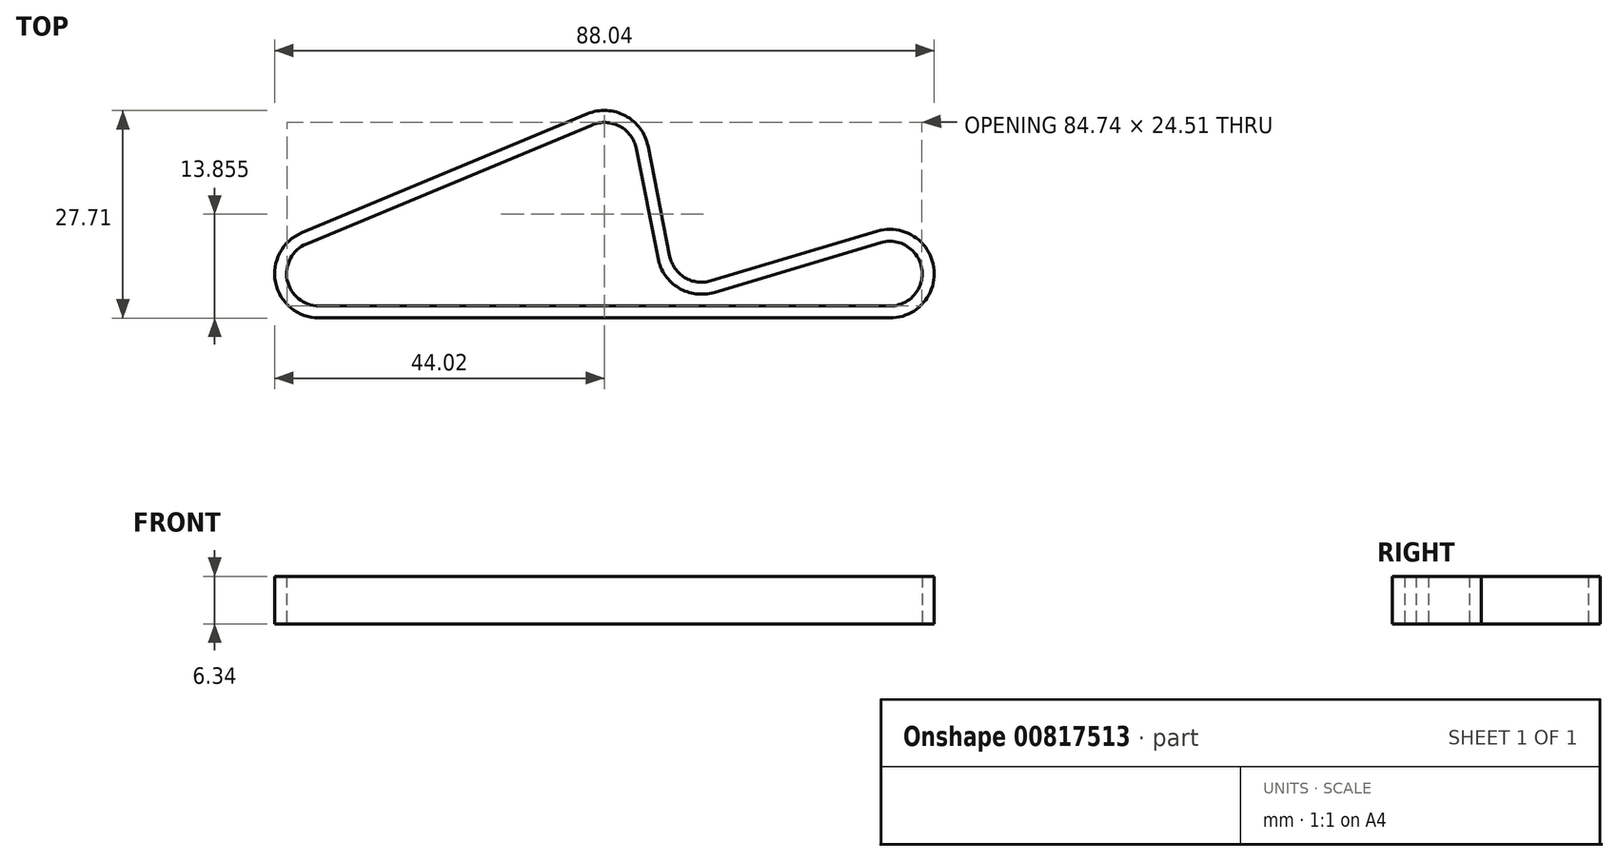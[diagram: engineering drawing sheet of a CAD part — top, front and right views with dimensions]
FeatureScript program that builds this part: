
annotation { "Feature Type Name" : "Feature", "Feature Type Description" : "" }
export const myFeature = defineFeature(function(context is Context, id is Id, definition is map)
    precondition{}
    {
        {
            var Q0;
            Q0=qCreatedBy(makeId("Top.planeOp"),FACE);
            var sketch = newSketch(context, id + "F0", { "sketchPlane" : qUnion([Q0])});
            skCircle(sketch, "E0", {"center": v(-38.1, 0) * mm, "radius": 4.32 * mm, "construction": true});
            skArc(sketch, "E1", {"start": v(34.14, 1.72) * mm, "mid": v(40.97, -3.23) * mm, "end": v(36.86, 4.14) * mm, "construction": true});
            skArc(sketch, "E2", {"start": v(4.24, 16.71) * mm, "mid": v(-3.73, 18.04) * mm, "end": v(1.37, 11.78) * mm, "construction": true});
            skLineSegment(sketch, "E3", {"start": v(-38.1, -4.32) * mm, "end": v(38.1, -4.32) * mm});
            skLineSegment(sketch, "E4", {"start": v(-39.76, 3.99) * mm, "end": v(-1.66, 19.86) * mm});
            skArc(sketch, "E5", {"start": v(-39.76, 3.99) * mm, "mid": v(-42.33, -0.85) * mm, "end": v(-38.1, -4.32) * mm});
            skArc(sketch, "E6", {"start": v(4.24, 16.71) * mm, "mid": v(2.03, 19.68) * mm, "end": v(-1.66, 19.86) * mm});
            skArc(sketch, "E7", {"start": v(38.1, -4.32) * mm, "mid": v(42.37, 0.62) * mm, "end": v(36.86, 4.14) * mm});
            skLineSegment(sketch, "E8.0", {"start": v(-40.38, 5.46) * mm, "end": v(-2.28, 21.34) * mm});
            skLineSegment(sketch, "E8.1", {"start": v(-38.1, -5.92) * mm, "end": v(38.1, -5.92) * mm});
            skArc(sketch, "E8.2", {"start": v(38.1, -5.92) * mm, "mid": v(43.96, 0.86) * mm, "end": v(36.4, 5.67) * mm});
            skArc(sketch, "E8.3", {"start": v(-40.38, 5.46) * mm, "mid": v(-43.9, -1.16) * mm, "end": v(-38.1, -5.92) * mm});
            skArc(sketch, "E8.5", {"start": v(5.8, 17.03) * mm, "mid": v(2.79, 21.1) * mm, "end": v(-2.28, 21.34) * mm});
            skCircle(sketch, "E9", {"center": v(12.95, 3.17) * mm, "radius": 4.32 * mm, "construction": true});
            skArc(sketch, "E10", {"start": v(8.72, 2.34) * mm, "mid": v(10.72, -0.52) * mm, "end": v(14.19, -0.96) * mm});
            skLineSegment(sketch, "E11", {"start": v(5.8, 17.03) * mm, "end": v(8.72, 2.34) * mm});
            skLineSegment(sketch, "E12", {"start": v(36.4, 5.67) * mm, "end": v(14.19, -0.96) * mm});
            skLineSegment(sketch, "E13", {"start": v(4.24, 16.71) * mm, "end": v(7.15, 2.02) * mm});
            skLineSegment(sketch, "E14", {"start": v(36.86, 4.14) * mm, "end": v(14.65, -2.5) * mm});
            skArc(sketch, "E15", {"start": v(7.15, 2.02) * mm, "mid": v(9.9, -1.9) * mm, "end": v(14.65, -2.5) * mm});
            skSolve(sketch);
        }
        {
            var Q0;
            Q0=makeQuery(id+"F0.imprint","IMPRINT",FACE,{"disambiguationData":[TD([[makeQuery(id+"F0.imprint","IMPRINT",EDGE,{"derivedFrom":sQuery(id+"F0.wireOp",EDGE,"E3")}),-1.0]])]});
            extrude(context, id + "F1", {"entities" : qUnion([Q0]), "endBound" : BoundingType.SYMMETRIC, "depth" : 6.35 * mm, "offsetDistance" : 25.4 * mm});
        }
    });
